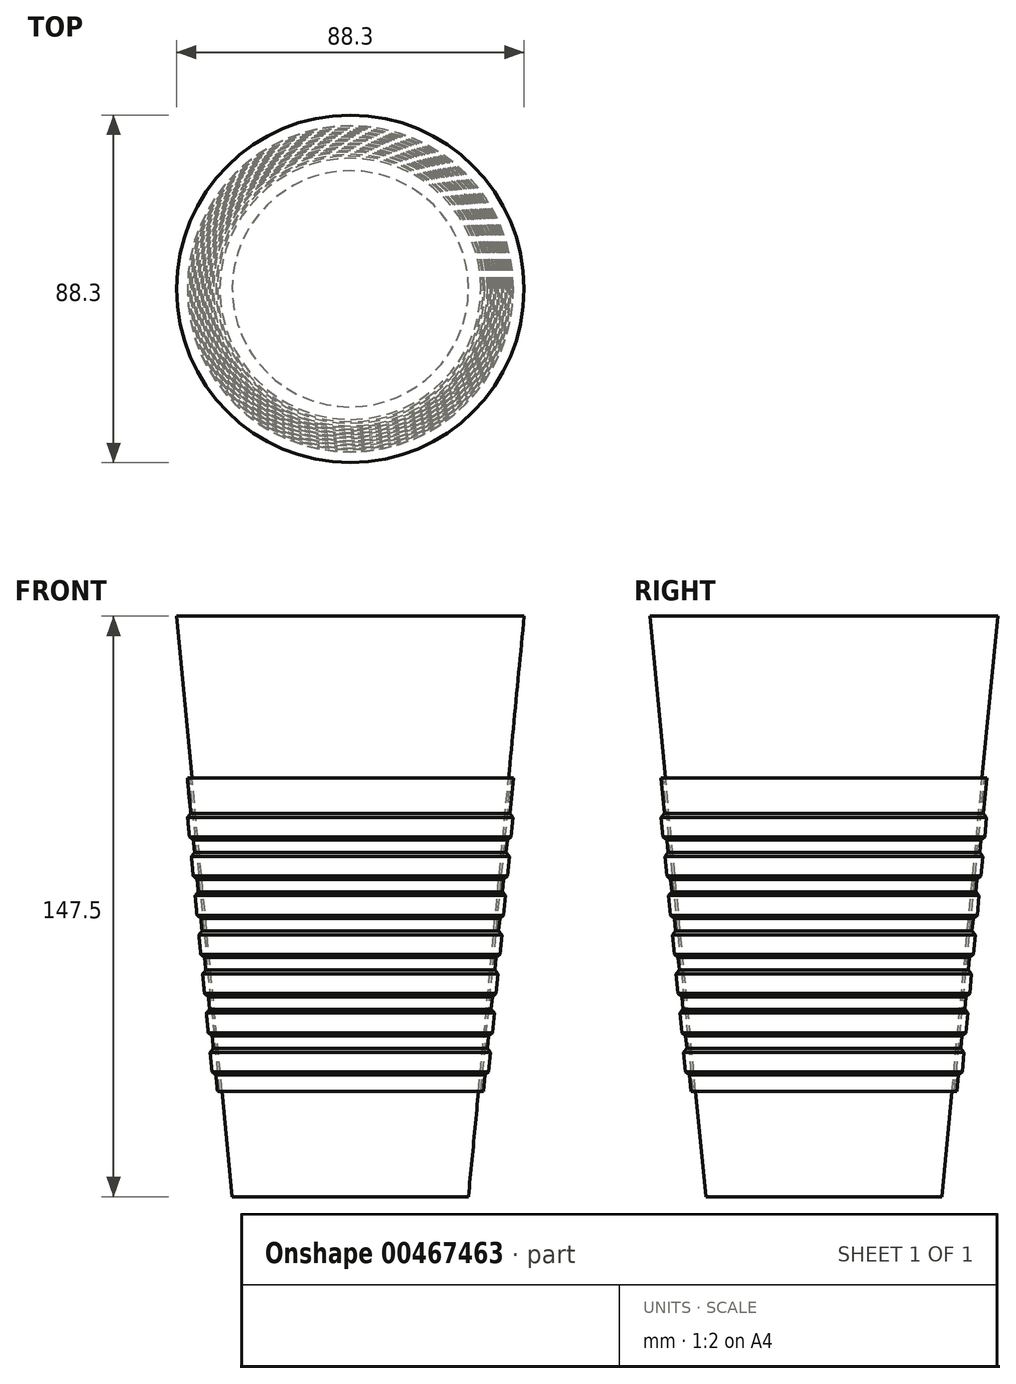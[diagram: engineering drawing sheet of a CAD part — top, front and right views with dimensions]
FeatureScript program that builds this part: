
annotation { "Feature Type Name" : "Feature", "Feature Type Description" : "" }
export const myFeature = defineFeature(function(context is Context, id is Id, definition is map)
    precondition{}
    {
        {
            var Q0;
            Q0=qCreatedBy(makeId("Top.planeOp"),FACE);
            var sketch = newSketch(context, id + "F0", { "sketchPlane" : qUnion([Q0])});
            skCircle(sketch, "E0", {"center": v(0, 0) * mm, "radius": 30 * mm});
            skSolve(sketch);
        }
        {
            var Q0;
            Q0=qCreatedBy(makeId("Top.planeOp"),FACE);
            cPlane(context, id + "F1", {"entities" : qUnion([Q0]), "cplaneType" : CPlaneType.OFFSET, "offset" : 147.5 * mm, "width" : 150 * mm, "height" : 150 * mm});
        }
        {
            var Q0;
            Q0=qCreatedBy(id+"F1.planeOp",FACE);
            var sketch = newSketch(context, id + "F2", { "sketchPlane" : qUnion([Q0])});
            skCircle(sketch, "E1", {"center": v(0, 0) * mm, "radius": 44.15 * mm});
            skSolve(sketch);
        }
        {
            var Q0;
            Q0=makeQuery(id+"F0.imprint","IMPRINT",FACE,{"disambiguationData":[TD([[makeQuery(id+"F0.imprint","IMPRINT",EDGE,{"derivedFrom":sQuery(id+"F0.wireOp",EDGE,"E0")}),1.0]])]});
            var Q1;
            Q1=makeQuery(id+"F2.imprint","IMPRINT",FACE,{"disambiguationData":[TD([[makeQuery(id+"F2.imprint","IMPRINT",EDGE,{"derivedFrom":sQuery(id+"F2.wireOp",EDGE,"E1")}),1.0]])]});
            loft(context, id + "F3", {"sheetProfilesArray" : [{ "sheetProfileEntities" : qUnion([Q0]) }, { "sheetProfileEntities" : qUnion([Q1]) }]});
        }
        {
            var Q0;
            Q0=qCreatedBy(makeId("Front.planeOp"),FACE);
            var sketch = newSketch(context, id + "F4", { "sketchPlane" : qUnion([Q0])});
            skLineSegment(sketch, "E2", {"start": v(44.15, 147.5) * mm, "end": v(30, 0) * mm, "construction": true});
            skLineSegment(sketch, "E3", {"start": v(-30, 0) * mm, "end": v(-44.15, 147.5) * mm, "construction": true});
            skLineSegment(sketch, "E4", {"start": v(0, 0) * mm, "end": v(0, 147.5) * mm, "construction": true});
            skLineSegment(sketch, "E5", {"start": v(-40.21, 106.44) * mm, "end": v(-40.81, 106.44) * mm, "construction": true});
            skLineSegment(sketch, "E6", {"start": v(-40.81, 106.44) * mm, "end": v(-33.18, 26.86) * mm});
            skLineSegment(sketch, "E7", {"start": v(-33.18, 26.86) * mm, "end": v(-33.77, 26.8) * mm});
            skLineSegment(sketch, "E8", {"start": v(-33.77, 26.8) * mm, "end": v(-41.41, 106.44) * mm});
            skLineSegment(sketch, "E9", {"start": v(-41.41, 106.44) * mm, "end": v(-40.81, 106.44) * mm});
            skLineSegment(sketch, "E10", {"start": v(-41.41, 106.44) * mm, "end": v(-40.46, 96.48) * mm, "construction": true});
            skLineSegment(sketch, "E11", {"start": v(-40.46, 96.48) * mm, "end": v(-41.35, 96.4) * mm, "construction": true});
            skLineSegment(sketch, "E12", {"start": v(-41.35, 96.4) * mm, "end": v(-40.87, 91.42) * mm});
            skLineSegment(sketch, "E13", {"start": v(-40.87, 91.42) * mm, "end": v(-39.9, 90.6) * mm});
            skLineSegment(sketch, "E14", {"start": v(-41.35, 96.4) * mm, "end": v(-40.54, 97.38) * mm});
            skLineSegment(sketch, "E15.1.0.0", {"start": v(-40.4, 86.44) * mm, "end": v(-39.59, 87.42) * mm});
            skLineSegment(sketch, "E15.1.0.1", {"start": v(-40.4, 86.44) * mm, "end": v(-39.92, 81.46) * mm});
            skLineSegment(sketch, "E15.1.0.2", {"start": v(-39.92, 81.46) * mm, "end": v(-38.94, 80.65) * mm});
            skLineSegment(sketch, "E15.2.0.0", {"start": v(-39.44, 76.49) * mm, "end": v(-38.63, 77.47) * mm});
            skLineSegment(sketch, "E15.2.0.1", {"start": v(-39.44, 76.49) * mm, "end": v(-38.96, 71.5) * mm});
            skLineSegment(sketch, "E15.2.0.2", {"start": v(-38.96, 71.5) * mm, "end": v(-37.98, 70.7) * mm});
            skLineSegment(sketch, "E15.3.0.0", {"start": v(-38.49, 66.53) * mm, "end": v(-37.68, 67.51) * mm});
            skLineSegment(sketch, "E15.3.0.1", {"start": v(-38.49, 66.53) * mm, "end": v(-38, 61.56) * mm});
            skLineSegment(sketch, "E15.3.0.2", {"start": v(-38, 61.56) * mm, "end": v(-37.03, 60.75) * mm});
            skLineSegment(sketch, "E15.direction1", {"start": v(-41.35, 96.4) * mm, "end": v(-40.4, 86.44) * mm, "construction": true});
            skLineSegment(sketch, "E16.0.4.0", {"start": v(-37.53, 56.58) * mm, "end": v(-36.72, 57.56) * mm});
            skLineSegment(sketch, "E16.3.4.0", {"start": v(-37.53, 56.58) * mm, "end": v(-37.05, 51.6) * mm});
            skLineSegment(sketch, "E16.6.4.0", {"start": v(-37.05, 51.6) * mm, "end": v(-36.07, 50.8) * mm});
            skLineSegment(sketch, "E17.0.5.0", {"start": v(-36.58, 46.62) * mm, "end": v(-35.77, 47.6) * mm});
            skLineSegment(sketch, "E17.3.5.0", {"start": v(-36.58, 46.62) * mm, "end": v(-36.1, 41.65) * mm});
            skLineSegment(sketch, "E17.6.5.0", {"start": v(-36.1, 41.65) * mm, "end": v(-35.12, 40.84) * mm});
            skLineSegment(sketch, "E17.0.6.0", {"start": v(-35.62, 36.67) * mm, "end": v(-34.81, 37.65) * mm});
            skLineSegment(sketch, "E17.3.6.0", {"start": v(-35.62, 36.67) * mm, "end": v(-35.14, 31.7) * mm});
            skLineSegment(sketch, "E17.6.6.0", {"start": v(-35.14, 31.7) * mm, "end": v(-34.16, 30.88) * mm});
            skSolve(sketch);
        }
        {
            var Q0;
            Q0=makeQuery(id+"F4.imprint","IMPRINT",FACE,{"disambiguationData":[TD([[makeQuery(id+"F4.imprint","IMPRINT",EDGE,{"derivedFrom":sQuery(id+"F4.wireOp",EDGE,"E12")}),1.0]])]});
            var Q1;
            Q1=makeQuery(id+"F4.imprint","IMPRINT",FACE,{"disambiguationData":[TD([[makeQuery(id+"F4.imprint","IMPRINT",EDGE,{"derivedFrom":sQuery(id+"F4.wireOp",EDGE,"E6")}),-1.0]])]});
            var Q2;
            {var subQ0=sQuery(id+"F4.wireOp",EDGE,"E15.1.0.0");Q2=makeQuery(id+"F4.imprint","IMPRINT",FACE,{"disambiguationData":[TD([[makeQuery(id+"F4.imprint","IMPRINT",EDGE,{"derivedFrom":subQ0}),-1.0]])]});}
            var Q3;
            {var subQ0=sQuery(id+"F4.wireOp",EDGE,"E15.3.0.0");Q3=makeQuery(id+"F4.imprint","IMPRINT",FACE,{"disambiguationData":[TD([[makeQuery(id+"F4.imprint","IMPRINT",EDGE,{"derivedFrom":subQ0}),-1.0]])]});}
            var Q4;
            {var subQ0=sQuery(id+"F4.wireOp",EDGE,"E15.2.0.0");Q4=makeQuery(id+"F4.imprint","IMPRINT",FACE,{"disambiguationData":[TD([[makeQuery(id+"F4.imprint","IMPRINT",EDGE,{"derivedFrom":subQ0}),-1.0]])]});}
            var Q5;
            {var subQ0=sQuery(id+"F4.wireOp",EDGE,"E16.0.4.0");Q5=makeQuery(id+"F4.imprint","IMPRINT",FACE,{"disambiguationData":[TD([[makeQuery(id+"F4.imprint","IMPRINT",EDGE,{"derivedFrom":subQ0}),-1.0]])]});}
            var Q6;
            {var subQ0=sQuery(id+"F4.wireOp",EDGE,"E17.0.5.0");Q6=makeQuery(id+"F4.imprint","IMPRINT",FACE,{"disambiguationData":[TD([[makeQuery(id+"F4.imprint","IMPRINT",EDGE,{"derivedFrom":subQ0}),-1.0]])]});}
            var Q7;
            {var subQ0=sQuery(id+"F4.wireOp",EDGE,"E17.0.6.0");Q7=makeQuery(id+"F4.imprint","IMPRINT",FACE,{"disambiguationData":[TD([[makeQuery(id+"F4.imprint","IMPRINT",EDGE,{"derivedFrom":subQ0}),-1.0]])]});}
            var Q8;
            Q8=sQuery(id+"F4.wireOp",EDGE,"E4");
            revolve(context, id + "F5", {"entities" : qUnion([Q0, Q1, Q2, Q3, Q4, Q5, Q6, Q7]), "axis" : qUnion([Q8]), "revolveType" : RevolveType.FULL});
        }
    });
